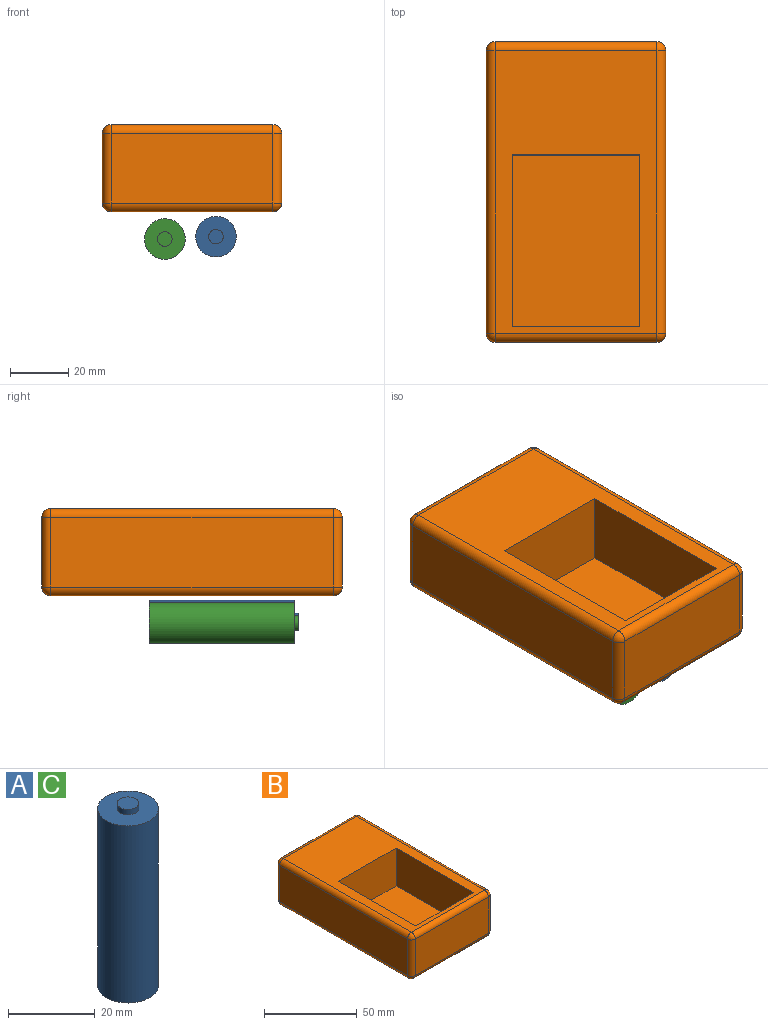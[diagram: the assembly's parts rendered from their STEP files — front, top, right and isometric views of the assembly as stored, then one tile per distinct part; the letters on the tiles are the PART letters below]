
ASSEMBLY  parts=3 mates=1
PART A: 5 faces, bbox 14x14x51.5 mm
  f0: cylinder r=7mm len=50mm, axis (0,0,-1), area 2199.1mm2, adj f1,f2
  f1: plane 14x14mm, normal (0,0,1), area 134.3mm2, adj f0,f3
  f2: plane 14x14mm, normal (0,0,-1), area 153.9mm2, adj f0
  f3: cylinder r=2.5mm len=5mm, axis (0,0,-1), area 23.6mm2, adj f1,f4
  f4: plane 5x5mm, normal (0,0,1), area 19.6mm2, adj f3
PART B: 31 faces, bbox 61.8x103.5x30 mm
  f0: plane 97.5x55.8mm, normal (0,0,1), area 2844.5mm2, adj f9,f10,f19,f20,f26,f27,f28,f29
  f1: plane 55.8x24mm, normal (0,-1,0), area 1339.2mm2, adj f14,f19,f22,f25
  f2: plane 97.5x24mm, normal (1,0,0), area 2340mm2, adj f11,f20,f21,f25
  f3: plane 55.8x24mm, normal (0,1,0), area 1339.2mm2, adj f6,f10,f11,f12
  f4: plane 97.5x24mm, normal (-1,0,0), area 2340mm2, adj f6,f9,f13,f14
  f5: plane 97.5x55.8mm, normal (0,0,-1), area 5440.5mm2, adj f12,f13,f21,f22
  f6: cylinder r=3mm len=24mm, axis (0,0,1), area 113.1mm2, adj f3,f4,f7,f8
  f7: sphere r=3mm, area 14.1mm2, adj f6,f9,f10
  f8: sphere r=3mm, area 14.1mm2, adj f6,f12,f13
  f9: cylinder r=3mm len=97.5mm, axis (0,1,0), area 459.5mm2, adj f0,f4,f7,f15
  f10: cylinder r=3mm len=55.8mm, axis (1,0,0), area 263mm2, adj f0,f3,f7,f16
  f11: cylinder r=3mm len=24mm, axis (0,0,-1), area 113.1mm2, adj f2,f3,f16,f17
  f12: cylinder r=3mm len=55.8mm, axis (-1,0,0), area 263mm2, adj f3,f5,f8,f17
  f13: cylinder r=3mm len=97.5mm, axis (0,-1,0), area 459.5mm2, adj f4,f5,f8,f18
  f14: cylinder r=3mm len=24mm, axis (0,0,-1), area 113.1mm2, adj f1,f4,f15,f18
  f15: sphere r=3mm, area 14.1mm2, adj f9,f14,f19
  f16: sphere r=3mm, area 14.1mm2, adj f10,f11,f20
  f17: sphere r=3mm, area 14.1mm2, adj f11,f12,f21
  f18: sphere r=3mm, area 14.1mm2, adj f13,f14,f22
  f19: cylinder r=3mm len=55.8mm, axis (-1,0,0), area 263mm2, adj f0,f1,f15,f23
  f20: cylinder r=3mm len=97.5mm, axis (0,-1,0), area 459.5mm2, adj f0,f2,f16,f23
  f21: cylinder r=3mm len=97.5mm, axis (0,1,0), area 459.5mm2, adj f2,f5,f17,f24
  f22: cylinder r=3mm len=55.8mm, axis (1,0,0), area 263mm2, adj f1,f5,f18,f24
  f23: sphere r=3mm, area 14.1mm2, adj f19,f20,f25
  f24: sphere r=3mm, area 14.1mm2, adj f21,f22,f25
  f25: cylinder r=3mm len=24mm, axis (0,0,1), area 113.1mm2, adj f1,f2,f23,f24
  f26: plane 59x25mm, normal (-1,0,0), area 1475mm2, adj f0,f27,f29,f30
  f27: plane 44x25mm, normal (0,-1,0), area 1100mm2, adj f0,f26,f28,f30
  f28: plane 59x25mm, normal (1,0,0), area 1475mm2, adj f0,f27,f29,f30
  f29: plane 44x25mm, normal (0,1,0), area 1100mm2, adj f0,f26,f28,f30
  f30: plane 59x44mm, normal (0,0,1), area 2596mm2, adj f26,f27,f28,f29
PART C: same geometry as A
PLACE A rot(axis=(0,0.71,-0.71),180deg) t=(8.26,14.73,-8.6)mm
PLACE B at identity fixed
PLACE C rot(axis=(0.79,0.43,-0.43),103.1deg) t=(-9.35,14.73,-9.41)mm
MATE planar A.f0 <-> C.f0  axis (0,1,0) through (8.26,14.73,-8.6)mm
